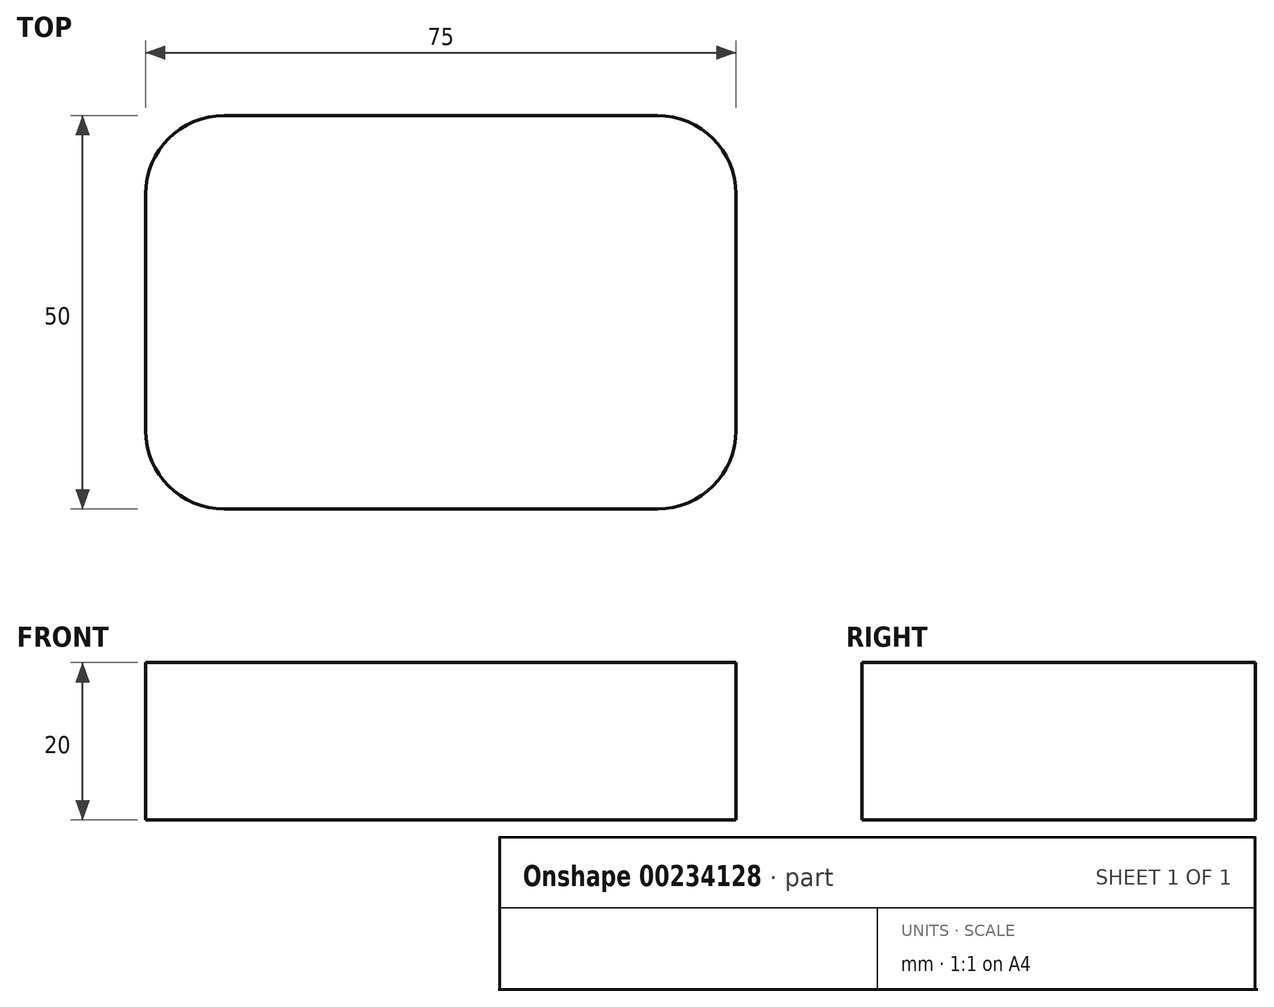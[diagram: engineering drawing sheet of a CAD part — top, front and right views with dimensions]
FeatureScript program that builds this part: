
annotation { "Feature Type Name" : "Feature", "Feature Type Description" : "" }
export const myFeature = defineFeature(function(context is Context, id is Id, definition is map)
    precondition{}
    {
        {
            var Q0;
            Q0=qCreatedBy(makeId("Top.planeOp"),FACE);
            var sketch = newSketch(context, id + "F0", { "sketchPlane" : qUnion([Q0])});
            skLineSegment(sketch, "E0.bottom", {"start": v(-27.5, -25) * mm, "end": v(27.5, -25) * mm});
            skLineSegment(sketch, "E0.top", {"start": v(-27.5, 25) * mm, "end": v(27.5, 25) * mm});
            skLineSegment(sketch, "E0.left", {"start": v(-37.5, -15) * mm, "end": v(-37.5, 15) * mm});
            skLineSegment(sketch, "E0.right", {"start": v(37.5, -15) * mm, "end": v(37.5, 15) * mm});
            skPoint(sketch, "E0.middle", {"position": v(0, 0) * mm});
            skPoint(sketch, "E1.visualSharp", {"position": v(-37.5, 25) * mm});
            skArc(sketch, "E1.filletArc", {"start": v(-27.5, 25) * mm, "mid": v(-34.57, 22.07) * mm, "end": v(-37.5, 15) * mm});
            skPoint(sketch, "E2.visualSharp", {"position": v(-37.5, -25) * mm});
            skArc(sketch, "E2.filletArc", {"start": v(-37.5, -15) * mm, "mid": v(-34.57, -22.07) * mm, "end": v(-27.5, -25) * mm});
            skPoint(sketch, "E3.visualSharp", {"position": v(37.5, -25) * mm});
            skArc(sketch, "E3.filletArc", {"start": v(27.5, -25) * mm, "mid": v(34.57, -22.07) * mm, "end": v(37.5, -15) * mm});
            skPoint(sketch, "E4.visualSharp", {"position": v(37.5, 25) * mm});
            skArc(sketch, "E4.filletArc", {"start": v(37.5, 15) * mm, "mid": v(34.57, 22.07) * mm, "end": v(27.5, 25) * mm});
            skSolve(sketch);
        }
        {
            var Q0;
            Q0 = qSketchRegion(id + "F0", true);
            extrude(context, id + "F1", {"entities" : qUnion([Q0]), "depth" : 20 * mm});
        }
    });
